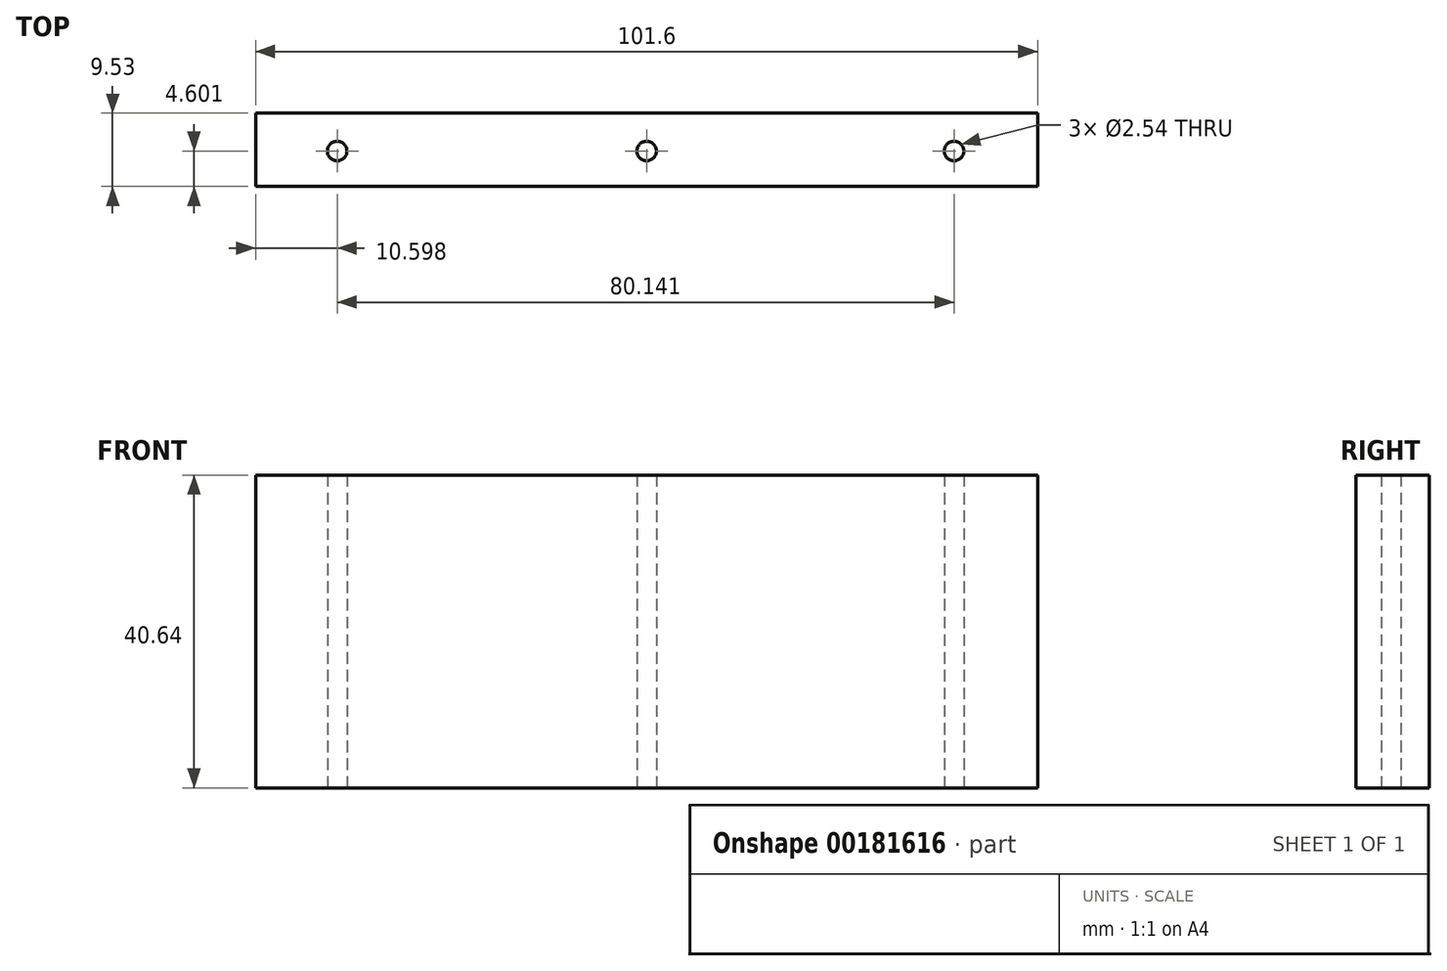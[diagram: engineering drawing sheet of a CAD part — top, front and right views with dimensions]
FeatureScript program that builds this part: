
annotation { "Feature Type Name" : "Feature", "Feature Type Description" : "" }
export const myFeature = defineFeature(function(context is Context, id is Id, definition is map)
    precondition{}
    {
        {
            var Q0;
            Q0=qCreatedBy(makeId("Front.planeOp"),FACE);
            var sketch = newSketch(context, id + "F0", { "sketchPlane" : qUnion([Q0])});
            skLineSegment(sketch, "E0.bottom", {"start": v(-50.8, 20.32) * mm, "end": v(50.8, 20.32) * mm});
            skLineSegment(sketch, "E0.top", {"start": v(-50.8, -20.32) * mm, "end": v(50.8, -20.32) * mm});
            skLineSegment(sketch, "E0.left", {"start": v(-50.8, 20.32) * mm, "end": v(-50.8, -20.32) * mm});
            skLineSegment(sketch, "E0.right", {"start": v(50.8, 20.32) * mm, "end": v(50.8, -20.32) * mm});
            skPoint(sketch, "E0.middle", {"position": v(0, 0) * mm});
            skSolve(sketch);
        }
        {
            var Q0;
            Q0 = qSketchRegion(id + "F0", true);
            extrude(context, id + "F1", {"entities" : qUnion([Q0]), "oppositeDirection" : true, "depth" : 9.52 * mm});
        }
        {
            var Q0;
            Q0=makeQuery(id+"F1.opExtrude","SWEPT_FACE",FACE,{"disambiguationData":[OSD([sQuery(id+"F0.wireOp",EDGE,"E0.top")])]});
            var sketch = newSketch(context, id + "F2", { "sketchPlane" : qUnion([Q0])});
            skCircle(sketch, "E1", {"center": v(-40.2, -4.6) * mm, "radius": 1.27 * mm});
            skCircle(sketch, "E2", {"center": v(0, -4.6) * mm, "radius": 1.27 * mm});
            skPoint(sketch, "E2.centerSnap0", {"position": v(0, -9.53) * mm});
            skCircle(sketch, "E3", {"center": v(39.94, -4.6) * mm, "radius": 1.27 * mm});
            skSolve(sketch);
        }
        {
            var Q0;
            Q0=makeQuery(id+"F2.imprint","IMPRINT",FACE,{"disambiguationData":[TD([[makeQuery(id+"F2.imprint","IMPRINT",EDGE,{"derivedFrom":sQuery(id+"F2.wireOp",EDGE,"E1")}),1.0]])]});
            var Q1;
            Q1=makeQuery(id+"F2.imprint","IMPRINT",FACE,{"disambiguationData":[TD([[makeQuery(id+"F2.imprint","IMPRINT",EDGE,{"derivedFrom":sQuery(id+"F2.wireOp",EDGE,"E2")}),1.0]])]});
            var Q2;
            Q2=makeQuery(id+"F2.imprint","IMPRINT",FACE,{"disambiguationData":[TD([[makeQuery(id+"F2.imprint","IMPRINT",EDGE,{"derivedFrom":sQuery(id+"F2.wireOp",EDGE,"E3")}),1.0]])]});
            extrude(context, id + "F3", {"entities" : qUnion([Q0, Q1, Q2]), "operationType" : NewBodyOperationType.REMOVE, "endBound" : BoundingType.THROUGH_ALL, "oppositeDirection" : true, "depth" : 25.4 * mm});
        }
    });
